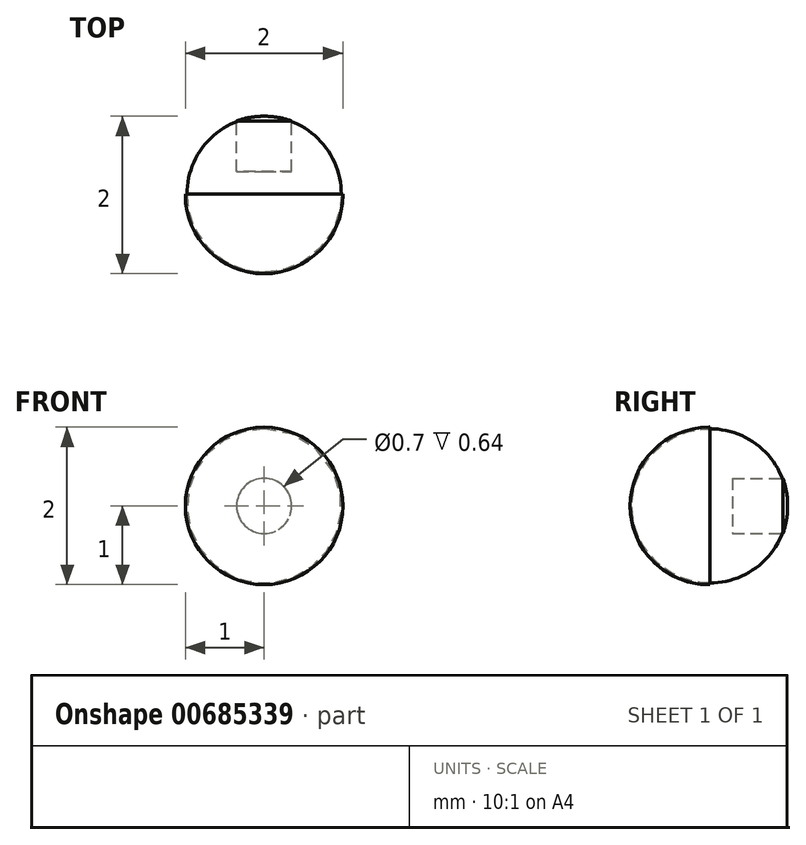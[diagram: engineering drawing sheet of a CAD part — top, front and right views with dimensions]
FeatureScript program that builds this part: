
annotation { "Feature Type Name" : "Feature", "Feature Type Description" : "" }
export const myFeature = defineFeature(function(context is Context, id is Id, definition is map)
    precondition{}
    {
        {
            var Q0;
            Q0=qCreatedBy(makeId("Front.planeOp"),FACE);
            var sketch = newSketch(context, id + "F0", { "sketchPlane" : qUnion([Q0])});
            skCircle(sketch, "E0", {"center": v(0, 0) * mm, "radius": 1 * mm});
            skSolve(sketch);
        }
        {
            var Q0;
            Q0 = qSketchRegion(id + "F0", true);
            extrude(context, id + "F1", {"entities" : qUnion([Q0]), "depth" : 2 * mm, "offsetDistance" : 25 * mm});
        }
        {
            var Q0;
            Q0=makeQuery(id+"F1.opExtrude","CAP_EDGE",EDGE,{"disambiguationData":[OSD([sQuery(id+"F0.wireOp",EDGE,"E0")])],"isStart":false});
            fillet(context, id + "F2", {"entities" : qUnion([Q0]), "radius" : 1 * mm, "tangentPropagation" : true, "allowEdgeOverflow" : false});
        }
        {
            var Q0;
            Q0=makeQuery(id+"F1.opExtrude","CAP_EDGE",EDGE,{"disambiguationData":[OSD([sQuery(id+"F0.wireOp",EDGE,"E0")])],"isStart":true});
            fillet(context, id + "F3", {"entities" : qUnion([Q0]), "radius" : 0.99 * mm, "tangentPropagation" : true, "allowEdgeOverflow" : false});
        }
        {
            var Q0;
            Q0=makeQuery(id+"F1.opExtrude","CAP_FACE",FACE,{"disambiguationData":[OSD([sQuery(id+"F0.wireOp",EDGE,"E0")])],"isStart":true});
            var sketch = newSketch(context, id + "F4", { "sketchPlane" : qUnion([Q0])});
            skCircle(sketch, "E1", {"center": v(0, 0) * mm, "radius": 0.35 * mm});
            skSolve(sketch);
        }
        {
            var Q0;
            Q0 = qSketchRegion(id + "F4", true);
            extrude(context, id + "F5", {"entities" : qUnion([Q0]), "operationType" : NewBodyOperationType.REMOVE, "oppositeDirection" : true, "depth" : 0.7 * mm, "offsetDistance" : 25 * mm});
        }
    });
